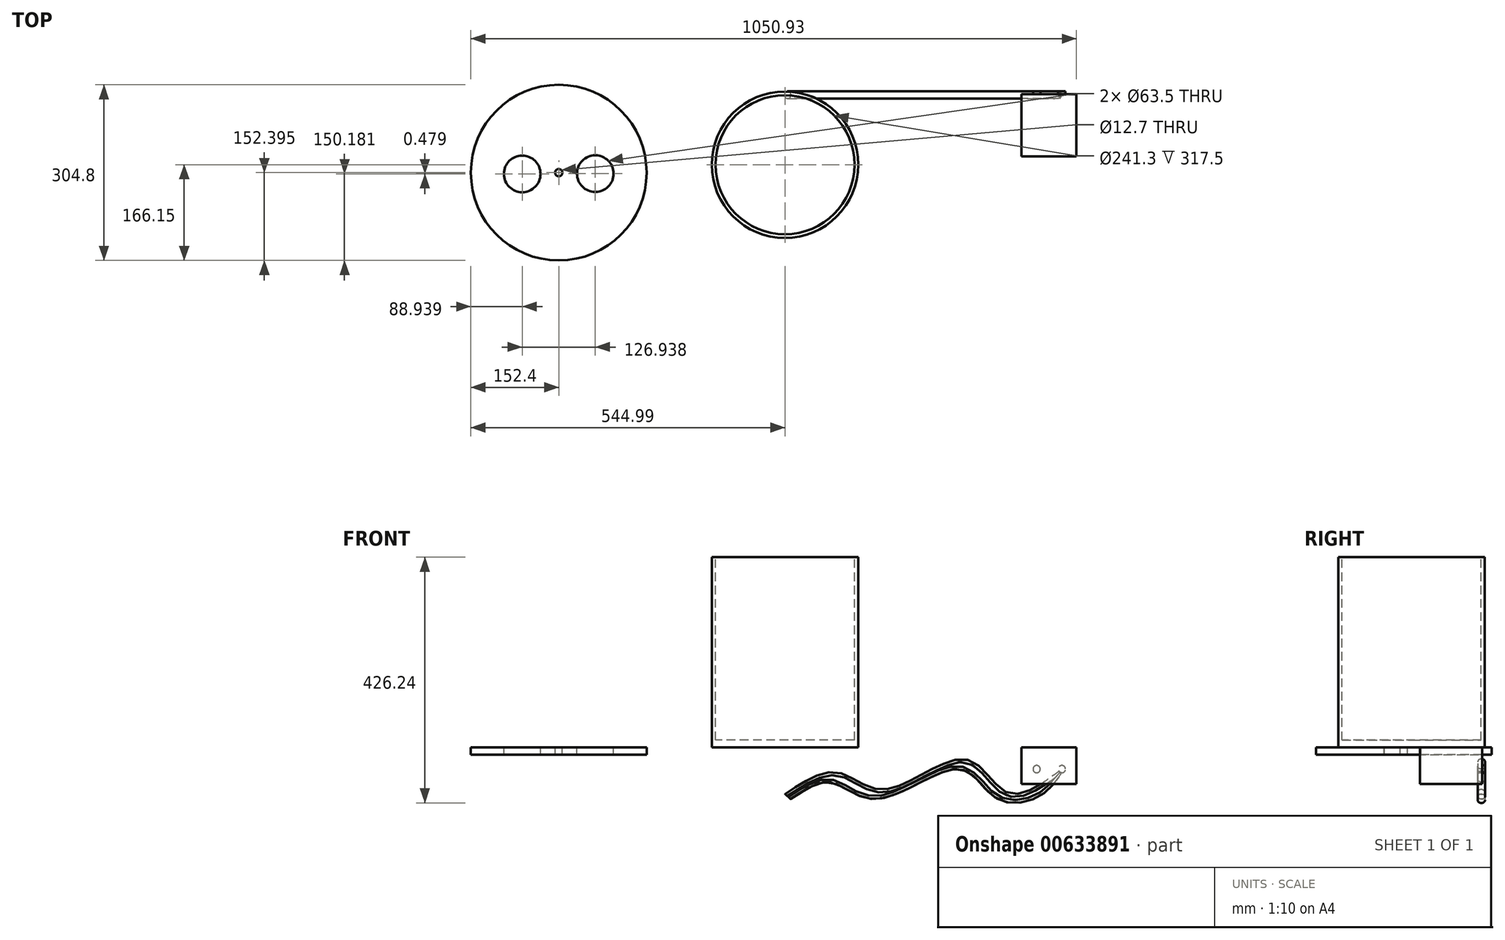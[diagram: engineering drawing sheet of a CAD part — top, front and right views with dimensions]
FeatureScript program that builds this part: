
annotation { "Feature Type Name" : "Feature", "Feature Type Description" : "" }
export const myFeature = defineFeature(function(context is Context, id is Id, definition is map)
    precondition{}
    {
        {
            var Q0;
            Q0=qCreatedBy(makeId("Top.planeOp"),FACE);
            var sketch = newSketch(context, id + "F0", { "sketchPlane" : qUnion([Q0])});
            skCircle(sketch, "E0", {"center": v(0, 0) * mm, "radius": 127 * mm});
            skSolve(sketch);
        }
        {
            var Q0;
            Q0 = qSketchRegion(id + "F0", true);
            extrude(context, id + "F1", {"entities" : qUnion([Q0]), "depth" : 330.2 * mm, "offsetDistance" : 25.4 * mm});
        }
        {
            var Q0;
            Q0=makeQuery(id+"F1.opExtrude","CAP_FACE",FACE,{"disambiguationData":[OSD([sQuery(id+"F0.wireOp",EDGE,"E0")])],"isStart":false});
            var sketch = newSketch(context, id + "F2", { "sketchPlane" : qUnion([Q0])});
            skCircle(sketch, "E1", {"center": v(0, 0) * mm, "radius": 120.65 * mm});
            skSolve(sketch);
        }
        {
            var Q0;
            Q0=makeQuery(id+"F2.imprint","IMPRINT",FACE,{"disambiguationData":[TD([[makeQuery(id+"F2.imprint","IMPRINT",EDGE,{"derivedFrom":sQuery(id+"F2.wireOp",EDGE,"E1")}),1.0]])]});
            extrude(context, id + "F3", {"entities" : qUnion([Q0]), "operationType" : NewBodyOperationType.REMOVE, "oppositeDirection" : true, "depth" : 317.5 * mm, "offsetDistance" : 25.4 * mm});
        }
        {
            var Q0;
            Q0=makeQuery(id+"F1.opExtrude","CAP_FACE",FACE,{"disambiguationData":[OSD([sQuery(id+"F0.wireOp",EDGE,"E0")])],"isStart":true});
            var sketch = newSketch(context, id + "F4", { "sketchPlane" : qUnion([Q0])});
            skCircle(sketch, "E2", {"center": v(-392.59, 13.75) * mm, "radius": 152.4 * mm});
            skSolve(sketch);
        }
        {
            var Q0;
            Q0 = qSketchRegion(id + "F4", true);
            extrude(context, id + "F5", {"entities" : qUnion([Q0]), "depth" : 12.7 * mm, "offsetDistance" : 25.4 * mm});
        }
        {
            var Q0;
            Q0=makeQuery(id+"F1.opExtrude","CAP_FACE",FACE,{"disambiguationData":[OSD([sQuery(id+"F0.wireOp",EDGE,"E0")])],"isStart":true});
            var sketch = newSketch(context, id + "F6", { "sketchPlane" : qUnion([Q0])});
            skLineSegment(sketch, "E3.bottom", {"start": v(410.69, -122.27) * mm, "end": v(505.94, -122.27) * mm});
            skLineSegment(sketch, "E3.top", {"start": v(410.69, -14.32) * mm, "end": v(505.94, -14.32) * mm});
            skLineSegment(sketch, "E3.left", {"start": v(410.69, -122.27) * mm, "end": v(410.69, -14.32) * mm});
            skLineSegment(sketch, "E3.right", {"start": v(505.94, -122.27) * mm, "end": v(505.94, -14.32) * mm});
            skSolve(sketch);
        }
        {
            var Q0;
            Q0 = qSketchRegion(id + "F6", true);
            extrude(context, id + "F7", {"entities" : qUnion([Q0]), "depth" : 63.5 * mm, "offsetDistance" : 25.4 * mm});
        }
        {
            var Q0;
            Q0=makeQuery(id+"F7.opExtrude","SWEPT_FACE",FACE,{"disambiguationData":[OSD([sQuery(id+"F6.wireOp",EDGE,"E3.bottom")])]});
            var sketch = newSketch(context, id + "F8", { "sketchPlane" : qUnion([Q0])});
            skCircle(sketch, "E4", {"center": v(-480.54, -37.46) * mm, "radius": 6.35 * mm});
            skCircle(sketch, "E5", {"center": v(-436.72, -37.46) * mm, "radius": 6.35 * mm});
            skSolve(sketch);
        }
        {
            var Q0;
            Q0 = qSketchRegion(id + "F8", true);
            extrude(context, id + "F9", {"entities" : qUnion([Q0]), "operationType" : NewBodyOperationType.ADD, "depth" : 5.08 * mm, "offsetDistance" : 25.4 * mm});
        }
        {
            var Q0;
            Q0=makeQuery(id+"F5.opExtrude","CAP_FACE",FACE,{"disambiguationData":[OSD([sQuery(id+"F4.wireOp",EDGE,"E2")])],"isStart":true});
            var sketch = newSketch(context, id + "F10", { "sketchPlane" : qUnion([Q0])});
            skCircle(sketch, "E6", {"center": v(-392.59, -13.75) * mm, "radius": 6.35 * mm});
            skSolve(sketch);
        }
        {
            var Q0;
            Q0=makeQuery(id+"F10.imprint","IMPRINT",FACE,{"disambiguationData":[TD([[makeQuery(id+"F10.imprint","IMPRINT",EDGE,{"derivedFrom":sQuery(id+"F10.wireOp",EDGE,"E6")}),-1.0]])]});
            var sketch = newSketch(context, id + "F11", { "sketchPlane" : qUnion([Q0])});
            skCircle(sketch, "E7", {"center": v(-456.05, -15.97) * mm, "radius": 31.75 * mm});
            skCircle(sketch, "E8", {"center": v(-329.11, -15.5) * mm, "radius": 31.75 * mm});
            skSolve(sketch);
        }
        {
            var Q0;
            Q0 = qSketchRegion(id + "F10", true);
            extrude(context, id + "F12", {"entities" : qUnion([Q0]), "operationType" : NewBodyOperationType.REMOVE, "oppositeDirection" : true, "depth" : 25.4 * mm, "offsetDistance" : 25.4 * mm});
        }
        {
            var Q0;
            Q0 = qSketchRegion(id + "F11", true);
            extrude(context, id + "F13", {"entities" : qUnion([Q0]), "operationType" : NewBodyOperationType.REMOVE, "oppositeDirection" : true, "depth" : 25.4 * mm, "offsetDistance" : 25.4 * mm});
        }
        {
            var Q0;
            Q0=makeQuery(id+"F9.opExtrude","CAP_FACE",FACE,{"disambiguationData":[OSD([sQuery(id+"F8.wireOp",EDGE,"E4")])],"isStart":false});
            var sketch = newSketch(context, id + "F14", { "sketchPlane" : qUnion([Q0])});
            skFitSpline(sketch, "E9", {"points": [v(-480.54, -37.46) * mm, v(-385.2, -78.36) * mm, v(-313.97, -20.66) * mm, v(-171.87, -72.87) * mm, v(-92.49, -43.39) * mm, v(0, -80.8) * mm], "startDerivative": vector(523.6, -390.27) * mm, "endDerivative": vector(497.69, -327.2) * mm});
            skLineSegment(sketch, "E10", {"start": v(0, -80.8) * mm, "end": v(-9.49, -89.23) * mm});
            skFitSpline(sketch, "E11", {"points": [v(-9.49, -89.23) * mm, v(-40.16, -70.65) * mm, v(-82.29, -60.94) * mm, v(-159.71, -89.23) * mm, v(-303.78, -37.54) * mm, v(-369.01, -89.23) * mm, v(-457.14, -73.38) * mm, v(-482.84, -37.46) * mm, v(-482.88, -37.46) * mm], "startDerivative": vector(-288.47, 184.86) * mm, "endDerivative": vector(-8.76, -4.97) * mm});
            skLineSegment(sketch, "E12", {"start": v(-482.84, -37.46) * mm, "end": v(-480.54, -37.46) * mm});
            skSolve(sketch);
        }
        {
            var Q0;
            {var subQ0=sQuery(id+"F14.wireOp",EDGE,"E10");Q0=makeQuery(id+"F14.imprint","IMPRINT",FACE,{"disambiguationData":[TD([[makeQuery(id+"F14.imprint","IMPRINT",EDGE,{"derivedFrom":subQ0}),-1.0]])]});}
            extrude(context, id + "F15", {"entities" : qUnion([Q0]), "oppositeDirection" : true, "depth" : 12.7 * mm, "offsetDistance" : 25.4 * mm});
        }
        {
            var Q0;
            Q0=makeQuery(id+"F15.opExtrude","CAP_EDGE",EDGE,{"disambiguationData":[OSD([sQuery(id+"F14.wireOp",EDGE,"E11")])],"isStart":true});
            var Q1;
            Q1=makeQuery(id+"F15.opExtrude","CAP_EDGE",EDGE,{"disambiguationData":[OSD([sQuery(id+"F14.wireOp",EDGE,"E9")])],"isStart":true});
            var Q2;
            Q2=makeQuery(id+"F15.opExtrude","CAP_EDGE",EDGE,{"disambiguationData":[OSD([sQuery(id+"F14.wireOp",EDGE,"E11")])],"isStart":false});
            var Q3;
            Q3=makeQuery(id+"F15.opExtrude","CAP_EDGE",EDGE,{"disambiguationData":[OSD([sQuery(id+"F14.wireOp",EDGE,"E9")])],"isStart":false});
            fillet(context, id + "F16", {"entities" : qUnion([Q0, Q1, Q2, Q3]), "radius" : 5.08 * mm, "tangentPropagation" : true, "allowEdgeOverflow" : false});
        }
    });
